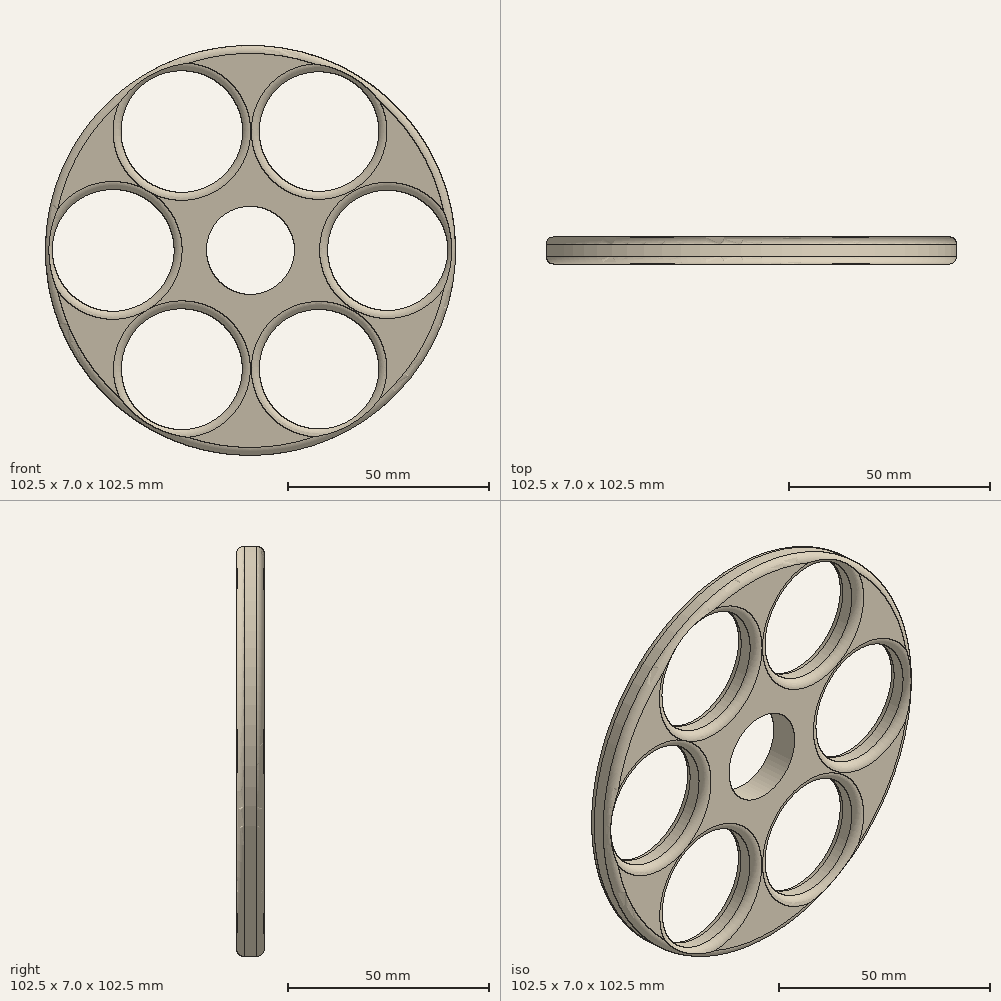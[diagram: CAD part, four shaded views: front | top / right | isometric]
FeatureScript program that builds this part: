
annotation { "Feature Type Name" : "Feature", "Feature Type Description" : "" }
export const myFeature = defineFeature(function(context is Context, id is Id, definition is map)
    precondition{}
    {
        {
            var Q0;
            Q0=qCreatedBy(makeId("Front.planeOp"),FACE);
            var sketch = newSketch(context, id + "F0", { "sketchPlane" : qUnion([Q0])});
            skCircle(sketch, "E0", {"center": v(0, 0) * mm, "radius": 11 * mm});
            skCircle(sketch, "E1.cCircle", {"center": v(0, 0) * mm, "radius": 56.23 * mm, "construction": true});
            skLineSegment(sketch, "E1.0", {"start": v(23.8, -56.23) * mm, "end": v(-23.8, -56.23) * mm});
            skLineSegment(sketch, "E1.1", {"start": v(-36.8, -48.73) * mm, "end": v(-60.6, -7.5) * mm});
            skLineSegment(sketch, "E1.2", {"start": v(-60.6, 7.5) * mm, "end": v(-36.8, 48.73) * mm});
            skLineSegment(sketch, "E1.3", {"start": v(-23.8, 56.23) * mm, "end": v(23.8, 56.23) * mm});
            skLineSegment(sketch, "E1.4", {"start": v(36.8, 48.73) * mm, "end": v(60.6, 7.5) * mm});
            skLineSegment(sketch, "E1.5", {"start": v(60.6, -7.5) * mm, "end": v(36.8, -48.73) * mm});
            skPoint(sketch, "E1.0.midPoint", {"position": v(0, -56.23) * mm});
            skLineSegment(sketch, "E2", {"start": v(-32.47, 56.23) * mm, "end": v(0, 0) * mm});
            skLineSegment(sketch, "E3", {"start": v(-64.93, 0) * mm, "end": v(0, 0) * mm});
            skLineSegment(sketch, "E4", {"start": v(-32.47, -56.23) * mm, "end": v(0, 0) * mm});
            skLineSegment(sketch, "E5", {"start": v(32.47, -56.23) * mm, "end": v(0, 0) * mm});
            skLineSegment(sketch, "E6", {"start": v(64.93, 0) * mm, "end": v(0, 0) * mm});
            skLineSegment(sketch, "E7", {"start": v(32.47, 56.23) * mm, "end": v(0, 0) * mm});
            skLineSegment(sketch, "E8", {"start": v(0, 56.23) * mm, "end": v(0, 0) * mm});
            skLineSegment(sketch, "E9", {"start": v(-48.7, 28.12) * mm, "end": v(0, 0) * mm});
            skLineSegment(sketch, "E10", {"start": v(-48.7, -28.12) * mm, "end": v(0, 0) * mm});
            skLineSegment(sketch, "E11", {"start": v(0, -56.23) * mm, "end": v(0, 0) * mm});
            skLineSegment(sketch, "E12", {"start": v(48.7, -28.12) * mm, "end": v(0, 0) * mm});
            skLineSegment(sketch, "E13", {"start": v(48.7, 28.12) * mm, "end": v(0, 0) * mm});
            skCircle(sketch, "E14.0", {"center": v(0, 0) * mm, "radius": 49.7 * mm});
            skCircle(sketch, "E15.0", {"center": v(0, 0) * mm, "radius": 34.3 * mm});
            skCircle(sketch, "E16", {"center": v(34.3, 0) * mm, "radius": 15.02 * mm});
            skCircle(sketch, "E17", {"center": v(17.15, 29.7) * mm, "radius": 14.94 * mm});
            skCircle(sketch, "E18", {"center": v(-17.15, 29.7) * mm, "radius": 15.2 * mm});
            skCircle(sketch, "E19", {"center": v(-34.3, 0) * mm, "radius": 15.22 * mm});
            skCircle(sketch, "E20", {"center": v(-17.15, -29.7) * mm, "radius": 15.1 * mm});
            skCircle(sketch, "E21", {"center": v(17.15, -29.7) * mm, "radius": 14.93 * mm});
            skPoint(sketch, "E22.visualSharp", {"position": v(32.47, 56.23) * mm});
            skArc(sketch, "E22.filletArc", {"start": v(36.8, 48.73) * mm, "mid": v(31.3, 54.22) * mm, "end": v(23.8, 56.23) * mm});
            skPoint(sketch, "E23.visualSharp", {"position": v(-32.47, 56.23) * mm});
            skArc(sketch, "E23.filletArc", {"start": v(-23.8, 56.23) * mm, "mid": v(-31.3, 54.22) * mm, "end": v(-36.8, 48.73) * mm});
            skPoint(sketch, "E24.visualSharp", {"position": v(-64.93, 0) * mm});
            skArc(sketch, "E24.filletArc", {"start": v(-60.6, 7.5) * mm, "mid": v(-62.61, 0) * mm, "end": v(-60.6, -7.5) * mm});
            skPoint(sketch, "E25.visualSharp", {"position": v(-32.47, -56.23) * mm});
            skArc(sketch, "E25.filletArc", {"start": v(-36.8, -48.73) * mm, "mid": v(-31.3, -54.22) * mm, "end": v(-23.8, -56.23) * mm});
            skPoint(sketch, "E26.visualSharp", {"position": v(32.47, -56.23) * mm});
            skArc(sketch, "E26.filletArc", {"start": v(23.8, -56.23) * mm, "mid": v(31.3, -54.22) * mm, "end": v(36.8, -48.73) * mm});
            skPoint(sketch, "E27.visualSharp", {"position": v(64.93, 0) * mm});
            skArc(sketch, "E27.filletArc", {"start": v(60.6, -7.5) * mm, "mid": v(62.61, 0) * mm, "end": v(60.6, 7.5) * mm});
            skCircle(sketch, "E28", {"center": v(0, 0) * mm, "radius": 51.25 * mm});
            skSolve(sketch);
        }
        {
            var Q0;
            Q0 = qSketchRegion(id + "F0", true);
            extrude(context, id + "F1", {"entities" : qUnion([Q0]), "depth" : 25 * mm, "offsetDistance" : 25 * mm});
        }
        {
            var Q0;
            {var subQ0=sQuery(id+"F0.wireOp",EDGE,"E14.0");var subQ1=sQuery(id+"F0.wireOp",EDGE,"E2");var subQ2=makeQuery(id+"F0.imprint","INTERSECT",VERTEX,{"derivedFrom":[subQ1,subQ0]});Q0=makeQuery(id+"F0.imprint","IMPRINT",FACE,{"disambiguationData":[TD([[makeQuery(id+"F0.imprint","IMPRINT",EDGE,{"disambiguationData":[TD([[subQ2,-1.0]])],"derivedFrom":subQ1}),-1.0]])]});}
            var Q1;
            {var subQ0=sQuery(id+"F0.wireOp",EDGE,"E14.0");var subQ1=sQuery(id+"F0.wireOp",EDGE,"E3");var subQ2=makeQuery(id+"F0.imprint","INTERSECT",VERTEX,{"derivedFrom":[subQ1,subQ0]});Q1=makeQuery(id+"F0.imprint","IMPRINT",FACE,{"disambiguationData":[TD([[makeQuery(id+"F0.imprint","IMPRINT",EDGE,{"disambiguationData":[TD([[subQ2,-1.0]])],"derivedFrom":subQ1}),1.0]])]});}
            var Q2;
            {var subQ5=sQuery(id+"F0.wireOp",EDGE,"E2");var subQ6=sQuery(id+"F0.wireOp",EDGE,"E0");var subQ7=makeQuery(id+"F0.imprint","INTERSECT",VERTEX,{"derivedFrom":[subQ6,subQ5]});Q2=makeQuery(id+"F0.imprint","IMPRINT",FACE,{"disambiguationData":[TD([[makeQuery(id+"F0.imprint","IMPRINT",EDGE,{"disambiguationData":[TD([[subQ7,-1.0]])],"derivedFrom":subQ6}),-1.0]])]});}
            var Q3;
            {var subQ1=sQuery(id+"F0.wireOp",EDGE,"E9");var subQ5=sQuery(id+"F0.wireOp",EDGE,"E0");var subQ6=makeQuery(id+"F0.imprint","INTERSECT",VERTEX,{"derivedFrom":[subQ5,subQ1]});Q3=makeQuery(id+"F0.imprint","IMPRINT",FACE,{"disambiguationData":[TD([[makeQuery(id+"F0.imprint","IMPRINT",EDGE,{"disambiguationData":[TD([[subQ6,-1.0]])],"derivedFrom":subQ5}),-1.0]])]});}
            var Q4;
            {var subQ1=sQuery(id+"F0.wireOp",EDGE,"E8");var subQ5=sQuery(id+"F0.wireOp",EDGE,"E0");var subQ6=makeQuery(id+"F0.imprint","INTERSECT",VERTEX,{"derivedFrom":[subQ5,subQ1]});Q4=makeQuery(id+"F0.imprint","IMPRINT",FACE,{"disambiguationData":[TD([[makeQuery(id+"F0.imprint","IMPRINT",EDGE,{"disambiguationData":[TD([[subQ6,-1.0]])],"derivedFrom":subQ5}),-1.0]])]});}
            var Q5;
            {var subQ5=sQuery(id+"F0.wireOp",EDGE,"E7");var subQ6=sQuery(id+"F0.wireOp",EDGE,"E0");var subQ7=makeQuery(id+"F0.imprint","INTERSECT",VERTEX,{"derivedFrom":[subQ6,subQ5]});Q5=makeQuery(id+"F0.imprint","IMPRINT",FACE,{"disambiguationData":[TD([[makeQuery(id+"F0.imprint","IMPRINT",EDGE,{"disambiguationData":[TD([[subQ7,-1.0]])],"derivedFrom":subQ6}),-1.0]])]});}
            var Q6;
            {var subQ0=sQuery(id+"F0.wireOp",EDGE,"E13");var subQ1=sQuery(id+"F0.wireOp",EDGE,"E0");var subQ2=makeQuery(id+"F0.imprint","INTERSECT",VERTEX,{"derivedFrom":[subQ1,subQ0]});Q6=makeQuery(id+"F0.imprint","IMPRINT",FACE,{"disambiguationData":[TD([[makeQuery(id+"F0.imprint","IMPRINT",EDGE,{"disambiguationData":[TD([[subQ2,-1.0]])],"derivedFrom":subQ1}),-1.0]])]});}
            var Q7;
            {var subQ1=sQuery(id+"F0.wireOp",EDGE,"E13");var subQ5=sQuery(id+"F0.wireOp",EDGE,"E0");var subQ6=makeQuery(id+"F0.imprint","INTERSECT",VERTEX,{"derivedFrom":[subQ5,subQ1]});Q7=makeQuery(id+"F0.imprint","IMPRINT",FACE,{"disambiguationData":[TD([[makeQuery(id+"F0.imprint","IMPRINT",EDGE,{"disambiguationData":[TD([[subQ6,1.0]])],"derivedFrom":subQ5}),-1.0]])]});}
            var Q8;
            {var subQ5=sQuery(id+"F0.wireOp",EDGE,"E14.0");var subQ7=sQuery(id+"F0.wireOp",EDGE,"E6");var subQ8=makeQuery(id+"F0.imprint","INTERSECT",VERTEX,{"derivedFrom":[subQ7,subQ5]});Q8=makeQuery(id+"F0.imprint","IMPRINT",FACE,{"disambiguationData":[TD([[makeQuery(id+"F0.imprint","IMPRINT",EDGE,{"disambiguationData":[TD([[subQ8,-1.0]])],"derivedFrom":subQ7}),-1.0]])]});}
            var Q9;
            {var subQ5=sQuery(id+"F0.wireOp",EDGE,"E14.0");var subQ7=sQuery(id+"F0.wireOp",EDGE,"E7");var subQ8=makeQuery(id+"F0.imprint","INTERSECT",VERTEX,{"derivedFrom":[subQ7,subQ5]});Q9=makeQuery(id+"F0.imprint","IMPRINT",FACE,{"disambiguationData":[TD([[makeQuery(id+"F0.imprint","IMPRINT",EDGE,{"disambiguationData":[TD([[subQ8,-1.0]])],"derivedFrom":subQ7}),1.0]])]});}
            var Q10;
            {var subQ5=sQuery(id+"F0.wireOp",EDGE,"E14.0");var subQ6=sQuery(id+"F0.wireOp",EDGE,"E7");var subQ7=makeQuery(id+"F0.imprint","INTERSECT",VERTEX,{"derivedFrom":[subQ6,subQ5]});Q10=makeQuery(id+"F0.imprint","IMPRINT",FACE,{"disambiguationData":[TD([[makeQuery(id+"F0.imprint","IMPRINT",EDGE,{"disambiguationData":[TD([[subQ7,-1.0]])],"derivedFrom":subQ6}),-1.0]])]});}
            var Q11;
            {var subQ5=sQuery(id+"F0.wireOp",EDGE,"E14.0");var subQ6=sQuery(id+"F0.wireOp",EDGE,"E2");var subQ7=makeQuery(id+"F0.imprint","INTERSECT",VERTEX,{"derivedFrom":[subQ6,subQ5]});Q11=makeQuery(id+"F0.imprint","IMPRINT",FACE,{"disambiguationData":[TD([[makeQuery(id+"F0.imprint","IMPRINT",EDGE,{"disambiguationData":[TD([[subQ7,-1.0]])],"derivedFrom":subQ6}),1.0]])]});}
            var Q12;
            {var subQ0=sQuery(id+"F0.wireOp",EDGE,"E14.0");var subQ1=sQuery(id+"F0.wireOp",EDGE,"E3");var subQ2=makeQuery(id+"F0.imprint","INTERSECT",VERTEX,{"derivedFrom":[subQ1,subQ0]});Q12=makeQuery(id+"F0.imprint","IMPRINT",FACE,{"disambiguationData":[TD([[makeQuery(id+"F0.imprint","IMPRINT",EDGE,{"disambiguationData":[TD([[subQ2,-1.0]])],"derivedFrom":subQ1}),-1.0]])]});}
            var Q13;
            {var subQ1=sQuery(id+"F0.wireOp",EDGE,"E0");var subQ7=sQuery(id+"F0.wireOp",EDGE,"E3");var subQ8=makeQuery(id+"F0.imprint","INTERSECT",VERTEX,{"derivedFrom":[subQ1,subQ7]});Q13=makeQuery(id+"F0.imprint","IMPRINT",FACE,{"disambiguationData":[TD([[makeQuery(id+"F0.imprint","IMPRINT",EDGE,{"disambiguationData":[TD([[subQ8,-1.0]])],"derivedFrom":subQ1}),-1.0]])]});}
            var Q14;
            {var subQ1=sQuery(id+"F0.wireOp",EDGE,"E10");var subQ5=sQuery(id+"F0.wireOp",EDGE,"E0");var subQ6=makeQuery(id+"F0.imprint","INTERSECT",VERTEX,{"derivedFrom":[subQ5,subQ1]});Q14=makeQuery(id+"F0.imprint","IMPRINT",FACE,{"disambiguationData":[TD([[makeQuery(id+"F0.imprint","IMPRINT",EDGE,{"disambiguationData":[TD([[subQ6,-1.0]])],"derivedFrom":subQ5}),-1.0]])]});}
            var Q15;
            {var subQ5=sQuery(id+"F0.wireOp",EDGE,"E14.0");var subQ6=sQuery(id+"F0.wireOp",EDGE,"E4");var subQ7=makeQuery(id+"F0.imprint","INTERSECT",VERTEX,{"derivedFrom":[subQ6,subQ5]});Q15=makeQuery(id+"F0.imprint","IMPRINT",FACE,{"disambiguationData":[TD([[makeQuery(id+"F0.imprint","IMPRINT",EDGE,{"disambiguationData":[TD([[subQ7,-1.0]])],"derivedFrom":subQ6}),1.0]])]});}
            var Q16;
            {var subQ5=sQuery(id+"F0.wireOp",EDGE,"E14.0");var subQ7=sQuery(id+"F0.wireOp",EDGE,"E4");var subQ8=makeQuery(id+"F0.imprint","INTERSECT",VERTEX,{"derivedFrom":[subQ7,subQ5]});Q16=makeQuery(id+"F0.imprint","IMPRINT",FACE,{"disambiguationData":[TD([[makeQuery(id+"F0.imprint","IMPRINT",EDGE,{"disambiguationData":[TD([[subQ8,-1.0]])],"derivedFrom":subQ7}),-1.0]])]});}
            var Q17;
            {var subQ5=sQuery(id+"F0.wireOp",EDGE,"E14.0");var subQ6=sQuery(id+"F0.wireOp",EDGE,"E5");var subQ7=makeQuery(id+"F0.imprint","INTERSECT",VERTEX,{"derivedFrom":[subQ6,subQ5]});Q17=makeQuery(id+"F0.imprint","IMPRINT",FACE,{"disambiguationData":[TD([[makeQuery(id+"F0.imprint","IMPRINT",EDGE,{"disambiguationData":[TD([[subQ7,-1.0]])],"derivedFrom":subQ6}),1.0]])]});}
            var Q18;
            {var subQ1=sQuery(id+"F0.wireOp",EDGE,"E0");var subQ6=sQuery(id+"F0.wireOp",EDGE,"E11");var subQ9=makeQuery(id+"F0.imprint","INTERSECT",VERTEX,{"derivedFrom":[subQ1,subQ6]});Q18=makeQuery(id+"F0.imprint","IMPRINT",FACE,{"disambiguationData":[TD([[makeQuery(id+"F0.imprint","IMPRINT",EDGE,{"disambiguationData":[TD([[subQ9,-1.0]])],"derivedFrom":subQ1}),-1.0]])]});}
            var Q19;
            {var subQ1=sQuery(id+"F0.wireOp",EDGE,"E0");var subQ5=sQuery(id+"F0.wireOp",EDGE,"E4");var subQ6=makeQuery(id+"F0.imprint","INTERSECT",VERTEX,{"derivedFrom":[subQ1,subQ5]});Q19=makeQuery(id+"F0.imprint","IMPRINT",FACE,{"disambiguationData":[TD([[makeQuery(id+"F0.imprint","IMPRINT",EDGE,{"disambiguationData":[TD([[subQ6,-1.0]])],"derivedFrom":subQ1}),-1.0]])]});}
            var Q20;
            {var subQ5=sQuery(id+"F0.wireOp",EDGE,"E0");var subQ7=sQuery(id+"F0.wireOp",EDGE,"E5");var subQ8=makeQuery(id+"F0.imprint","INTERSECT",VERTEX,{"derivedFrom":[subQ5,subQ7]});Q20=makeQuery(id+"F0.imprint","IMPRINT",FACE,{"disambiguationData":[TD([[makeQuery(id+"F0.imprint","IMPRINT",EDGE,{"disambiguationData":[TD([[subQ8,-1.0]])],"derivedFrom":subQ5}),-1.0]])]});}
            var Q21;
            {var subQ5=sQuery(id+"F0.wireOp",EDGE,"E6");var subQ6=sQuery(id+"F0.wireOp",EDGE,"E0");var subQ7=makeQuery(id+"F0.imprint","INTERSECT",VERTEX,{"derivedFrom":[subQ6,subQ5]});Q21=makeQuery(id+"F0.imprint","IMPRINT",FACE,{"disambiguationData":[TD([[makeQuery(id+"F0.imprint","IMPRINT",EDGE,{"disambiguationData":[TD([[subQ7,1.0]])],"derivedFrom":subQ6}),-1.0]])]});}
            var Q22;
            {var subQ5=sQuery(id+"F0.wireOp",EDGE,"E14.0");var subQ6=sQuery(id+"F0.wireOp",EDGE,"E6");var subQ7=makeQuery(id+"F0.imprint","INTERSECT",VERTEX,{"derivedFrom":[subQ6,subQ5]});Q22=makeQuery(id+"F0.imprint","IMPRINT",FACE,{"disambiguationData":[TD([[makeQuery(id+"F0.imprint","IMPRINT",EDGE,{"disambiguationData":[TD([[subQ7,-1.0]])],"derivedFrom":subQ6}),1.0]])]});}
            var Q23;
            {var subQ0=sQuery(id+"F0.wireOp",EDGE,"E14.0");var subQ1=sQuery(id+"F0.wireOp",EDGE,"E5");var subQ2=makeQuery(id+"F0.imprint","INTERSECT",VERTEX,{"derivedFrom":[subQ1,subQ0]});Q23=makeQuery(id+"F0.imprint","IMPRINT",FACE,{"disambiguationData":[TD([[makeQuery(id+"F0.imprint","IMPRINT",EDGE,{"disambiguationData":[TD([[subQ2,-1.0]])],"derivedFrom":subQ1}),-1.0]])]});}
            extrude(context, id + "F2", {"entities" : qUnion([Q0, Q1, Q2, Q3, Q4, Q5, Q6, Q7, Q8, Q9, Q10, Q11, Q12, Q13, Q14, Q15, Q16, Q17, Q18, Q19, Q20, Q21, Q22, Q23]), "operationType" : NewBodyOperationType.ADD, "depth" : 7 * mm, "offsetDistance" : 25 * mm});
        }
        {
            var Q0;
            Q0=makeQuery(id+"F1.opExtrude","CAP_FACE",FACE,{"disambiguationData":[OSD([sQuery(id+"F0.wireOp",EDGE,"E1.0"),sQuery(id+"F0.wireOp",EDGE,"E1.1"),sQuery(id+"F0.wireOp",EDGE,"E1.2"),sQuery(id+"F0.wireOp",EDGE,"E1.3"),sQuery(id+"F0.wireOp",EDGE,"E1.4"),sQuery(id+"F0.wireOp",EDGE,"E1.5"),sQuery(id+"F0.wireOp",EDGE,"E14.0"),sQuery(id+"F0.wireOp",EDGE,"E22.filletArc"),sQuery(id+"F0.wireOp",EDGE,"E23.filletArc"),sQuery(id+"F0.wireOp",EDGE,"E24.filletArc"),sQuery(id+"F0.wireOp",EDGE,"E25.filletArc"),sQuery(id+"F0.wireOp",EDGE,"E26.filletArc"),sQuery(id+"F0.wireOp",EDGE,"E27.filletArc")])],"isStart":false});
            extrude(context, id + "F3", {"entities" : qUnion([Q0]), "operationType" : NewBodyOperationType.REMOVE, "oppositeDirection" : true, "depth" : 25 * mm, "offsetDistance" : 25 * mm});
        }
        {
            var Q0;
            Q0 = qSketchRegion(id + "F0", true);
            var Q1;
            {var subQ0=sQuery(id+"F0.wireOp",EDGE,"E28");var subQ1=sQuery(id+"F0.wireOp",EDGE,"E2");var subQ2=makeQuery(id+"F0.imprint","INTERSECT",VERTEX,{"derivedFrom":[subQ1,subQ0]});Q1=makeQuery(id+"F0.imprint","IMPRINT",FACE,{"disambiguationData":[TD([[makeQuery(id+"F0.imprint","IMPRINT",EDGE,{"disambiguationData":[TD([[subQ2,-1.0]])],"derivedFrom":subQ1}),1.0]])]});}
            var Q2;
            {var subQ0=sQuery(id+"F0.wireOp",EDGE,"E28");var subQ1=sQuery(id+"F0.wireOp",EDGE,"E2");var subQ2=makeQuery(id+"F0.imprint","INTERSECT",VERTEX,{"derivedFrom":[subQ1,subQ0]});Q2=makeQuery(id+"F0.imprint","IMPRINT",FACE,{"disambiguationData":[TD([[makeQuery(id+"F0.imprint","IMPRINT",EDGE,{"disambiguationData":[TD([[subQ2,-1.0]])],"derivedFrom":subQ1}),-1.0]])]});}
            var Q3;
            {var subQ0=sQuery(id+"F0.wireOp",EDGE,"E28");var subQ1=sQuery(id+"F0.wireOp",EDGE,"E3");var subQ2=makeQuery(id+"F0.imprint","INTERSECT",VERTEX,{"derivedFrom":[subQ1,subQ0]});Q3=makeQuery(id+"F0.imprint","IMPRINT",FACE,{"disambiguationData":[TD([[makeQuery(id+"F0.imprint","IMPRINT",EDGE,{"disambiguationData":[TD([[subQ2,-1.0]])],"derivedFrom":subQ1}),1.0]])]});}
            var Q4;
            {var subQ0=sQuery(id+"F0.wireOp",EDGE,"E28");var subQ1=sQuery(id+"F0.wireOp",EDGE,"E3");var subQ2=makeQuery(id+"F0.imprint","INTERSECT",VERTEX,{"derivedFrom":[subQ1,subQ0]});Q4=makeQuery(id+"F0.imprint","IMPRINT",FACE,{"disambiguationData":[TD([[makeQuery(id+"F0.imprint","IMPRINT",EDGE,{"disambiguationData":[TD([[subQ2,-1.0]])],"derivedFrom":subQ1}),-1.0]])]});}
            var Q5;
            {var subQ0=sQuery(id+"F0.wireOp",EDGE,"E28");var subQ1=sQuery(id+"F0.wireOp",EDGE,"E7");var subQ2=makeQuery(id+"F0.imprint","INTERSECT",VERTEX,{"derivedFrom":[subQ1,subQ0]});Q5=makeQuery(id+"F0.imprint","IMPRINT",FACE,{"disambiguationData":[TD([[makeQuery(id+"F0.imprint","IMPRINT",EDGE,{"disambiguationData":[TD([[subQ2,-1.0]])],"derivedFrom":subQ1}),-1.0]])]});}
            var Q6;
            {var subQ0=sQuery(id+"F0.wireOp",EDGE,"E28");var subQ1=sQuery(id+"F0.wireOp",EDGE,"E7");var subQ2=makeQuery(id+"F0.imprint","INTERSECT",VERTEX,{"derivedFrom":[subQ1,subQ0]});Q6=makeQuery(id+"F0.imprint","IMPRINT",FACE,{"disambiguationData":[TD([[makeQuery(id+"F0.imprint","IMPRINT",EDGE,{"disambiguationData":[TD([[subQ2,-1.0]])],"derivedFrom":subQ1}),1.0]])]});}
            var Q7;
            {var subQ0=sQuery(id+"F0.wireOp",EDGE,"E28");var subQ1=sQuery(id+"F0.wireOp",EDGE,"E6");var subQ2=makeQuery(id+"F0.imprint","INTERSECT",VERTEX,{"derivedFrom":[subQ1,subQ0]});Q7=makeQuery(id+"F0.imprint","IMPRINT",FACE,{"disambiguationData":[TD([[makeQuery(id+"F0.imprint","IMPRINT",EDGE,{"disambiguationData":[TD([[subQ2,-1.0]])],"derivedFrom":subQ1}),-1.0]])]});}
            var Q8;
            {var subQ0=sQuery(id+"F0.wireOp",EDGE,"E28");var subQ1=sQuery(id+"F0.wireOp",EDGE,"E6");var subQ2=makeQuery(id+"F0.imprint","INTERSECT",VERTEX,{"derivedFrom":[subQ1,subQ0]});Q8=makeQuery(id+"F0.imprint","IMPRINT",FACE,{"disambiguationData":[TD([[makeQuery(id+"F0.imprint","IMPRINT",EDGE,{"disambiguationData":[TD([[subQ2,-1.0]])],"derivedFrom":subQ1}),1.0]])]});}
            var Q9;
            {var subQ0=sQuery(id+"F0.wireOp",EDGE,"E28");var subQ1=sQuery(id+"F0.wireOp",EDGE,"E5");var subQ2=makeQuery(id+"F0.imprint","INTERSECT",VERTEX,{"derivedFrom":[subQ1,subQ0]});Q9=makeQuery(id+"F0.imprint","IMPRINT",FACE,{"disambiguationData":[TD([[makeQuery(id+"F0.imprint","IMPRINT",EDGE,{"disambiguationData":[TD([[subQ2,-1.0]])],"derivedFrom":subQ1}),-1.0]])]});}
            var Q10;
            {var subQ0=sQuery(id+"F0.wireOp",EDGE,"E28");var subQ1=sQuery(id+"F0.wireOp",EDGE,"E5");var subQ2=makeQuery(id+"F0.imprint","INTERSECT",VERTEX,{"derivedFrom":[subQ1,subQ0]});Q10=makeQuery(id+"F0.imprint","IMPRINT",FACE,{"disambiguationData":[TD([[makeQuery(id+"F0.imprint","IMPRINT",EDGE,{"disambiguationData":[TD([[subQ2,-1.0]])],"derivedFrom":subQ1}),1.0]])]});}
            var Q11;
            {var subQ0=sQuery(id+"F0.wireOp",EDGE,"E28");var subQ1=sQuery(id+"F0.wireOp",EDGE,"E4");var subQ2=makeQuery(id+"F0.imprint","INTERSECT",VERTEX,{"derivedFrom":[subQ1,subQ0]});Q11=makeQuery(id+"F0.imprint","IMPRINT",FACE,{"disambiguationData":[TD([[makeQuery(id+"F0.imprint","IMPRINT",EDGE,{"disambiguationData":[TD([[subQ2,-1.0]])],"derivedFrom":subQ1}),-1.0]])]});}
            var Q12;
            {var subQ0=sQuery(id+"F0.wireOp",EDGE,"E28");var subQ1=sQuery(id+"F0.wireOp",EDGE,"E4");var subQ2=makeQuery(id+"F0.imprint","INTERSECT",VERTEX,{"derivedFrom":[subQ1,subQ0]});Q12=makeQuery(id+"F0.imprint","IMPRINT",FACE,{"disambiguationData":[TD([[makeQuery(id+"F0.imprint","IMPRINT",EDGE,{"disambiguationData":[TD([[subQ2,-1.0]])],"derivedFrom":subQ1}),1.0]])]});}
            extrude(context, id + "F4", {"entities" : qUnion([Q0, Q1, Q2, Q3, Q4, Q5, Q6, Q7, Q8, Q9, Q10, Q11, Q12]), "operationType" : NewBodyOperationType.REMOVE, "endBound" : BoundingType.THROUGH_ALL, "depth" : 25 * mm, "offsetDistance" : 25 * mm});
        }
        {
            var Q0;
            {var subQ0=sQuery(id+"F0.wireOp",EDGE,"E28");var subQ1=sQuery(id+"F0.wireOp",EDGE,"E2");var subQ2=makeQuery(id+"F0.imprint","INTERSECT",VERTEX,{"derivedFrom":[subQ1,subQ0]});Q0=makeQuery(id+"F0.imprint","IMPRINT",FACE,{"disambiguationData":[TD([[makeQuery(id+"F0.imprint","IMPRINT",EDGE,{"disambiguationData":[TD([[subQ2,-1.0]])],"derivedFrom":subQ1}),-1.0]])]});}
            var Q1;
            {var subQ0=sQuery(id+"F0.wireOp",EDGE,"E28");var subQ1=sQuery(id+"F0.wireOp",EDGE,"E2");var subQ2=makeQuery(id+"F0.imprint","INTERSECT",VERTEX,{"derivedFrom":[subQ1,subQ0]});Q1=makeQuery(id+"F0.imprint","IMPRINT",FACE,{"disambiguationData":[TD([[makeQuery(id+"F0.imprint","IMPRINT",EDGE,{"disambiguationData":[TD([[subQ2,-1.0]])],"derivedFrom":subQ1}),1.0]])]});}
            var Q2;
            {var subQ0=sQuery(id+"F0.wireOp",EDGE,"E28");var subQ1=sQuery(id+"F0.wireOp",EDGE,"E3");var subQ2=makeQuery(id+"F0.imprint","INTERSECT",VERTEX,{"derivedFrom":[subQ1,subQ0]});Q2=makeQuery(id+"F0.imprint","IMPRINT",FACE,{"disambiguationData":[TD([[makeQuery(id+"F0.imprint","IMPRINT",EDGE,{"disambiguationData":[TD([[subQ2,-1.0]])],"derivedFrom":subQ1}),1.0]])]});}
            var Q3;
            {var subQ0=sQuery(id+"F0.wireOp",EDGE,"E28");var subQ1=sQuery(id+"F0.wireOp",EDGE,"E3");var subQ2=makeQuery(id+"F0.imprint","INTERSECT",VERTEX,{"derivedFrom":[subQ1,subQ0]});Q3=makeQuery(id+"F0.imprint","IMPRINT",FACE,{"disambiguationData":[TD([[makeQuery(id+"F0.imprint","IMPRINT",EDGE,{"disambiguationData":[TD([[subQ2,-1.0]])],"derivedFrom":subQ1}),-1.0]])]});}
            var Q4;
            {var subQ0=sQuery(id+"F0.wireOp",EDGE,"E28");var subQ1=sQuery(id+"F0.wireOp",EDGE,"E4");var subQ2=makeQuery(id+"F0.imprint","INTERSECT",VERTEX,{"derivedFrom":[subQ1,subQ0]});Q4=makeQuery(id+"F0.imprint","IMPRINT",FACE,{"disambiguationData":[TD([[makeQuery(id+"F0.imprint","IMPRINT",EDGE,{"disambiguationData":[TD([[subQ2,-1.0]])],"derivedFrom":subQ1}),1.0]])]});}
            var Q5;
            {var subQ0=sQuery(id+"F0.wireOp",EDGE,"E28");var subQ1=sQuery(id+"F0.wireOp",EDGE,"E4");var subQ2=makeQuery(id+"F0.imprint","INTERSECT",VERTEX,{"derivedFrom":[subQ1,subQ0]});Q5=makeQuery(id+"F0.imprint","IMPRINT",FACE,{"disambiguationData":[TD([[makeQuery(id+"F0.imprint","IMPRINT",EDGE,{"disambiguationData":[TD([[subQ2,-1.0]])],"derivedFrom":subQ1}),-1.0]])]});}
            var Q6;
            {var subQ0=sQuery(id+"F0.wireOp",EDGE,"E28");var subQ1=sQuery(id+"F0.wireOp",EDGE,"E5");var subQ2=makeQuery(id+"F0.imprint","INTERSECT",VERTEX,{"derivedFrom":[subQ1,subQ0]});Q6=makeQuery(id+"F0.imprint","IMPRINT",FACE,{"disambiguationData":[TD([[makeQuery(id+"F0.imprint","IMPRINT",EDGE,{"disambiguationData":[TD([[subQ2,-1.0]])],"derivedFrom":subQ1}),1.0]])]});}
            var Q7;
            {var subQ0=sQuery(id+"F0.wireOp",EDGE,"E28");var subQ1=sQuery(id+"F0.wireOp",EDGE,"E5");var subQ2=makeQuery(id+"F0.imprint","INTERSECT",VERTEX,{"derivedFrom":[subQ1,subQ0]});Q7=makeQuery(id+"F0.imprint","IMPRINT",FACE,{"disambiguationData":[TD([[makeQuery(id+"F0.imprint","IMPRINT",EDGE,{"disambiguationData":[TD([[subQ2,-1.0]])],"derivedFrom":subQ1}),-1.0]])]});}
            var Q8;
            {var subQ0=sQuery(id+"F0.wireOp",EDGE,"E28");var subQ1=sQuery(id+"F0.wireOp",EDGE,"E6");var subQ2=makeQuery(id+"F0.imprint","INTERSECT",VERTEX,{"derivedFrom":[subQ1,subQ0]});Q8=makeQuery(id+"F0.imprint","IMPRINT",FACE,{"disambiguationData":[TD([[makeQuery(id+"F0.imprint","IMPRINT",EDGE,{"disambiguationData":[TD([[subQ2,-1.0]])],"derivedFrom":subQ1}),1.0]])]});}
            var Q9;
            {var subQ0=sQuery(id+"F0.wireOp",EDGE,"E28");var subQ1=sQuery(id+"F0.wireOp",EDGE,"E6");var subQ2=makeQuery(id+"F0.imprint","INTERSECT",VERTEX,{"derivedFrom":[subQ1,subQ0]});Q9=makeQuery(id+"F0.imprint","IMPRINT",FACE,{"disambiguationData":[TD([[makeQuery(id+"F0.imprint","IMPRINT",EDGE,{"disambiguationData":[TD([[subQ2,-1.0]])],"derivedFrom":subQ1}),-1.0]])]});}
            var Q10;
            {var subQ0=sQuery(id+"F0.wireOp",EDGE,"E28");var subQ1=sQuery(id+"F0.wireOp",EDGE,"E7");var subQ2=makeQuery(id+"F0.imprint","INTERSECT",VERTEX,{"derivedFrom":[subQ1,subQ0]});Q10=makeQuery(id+"F0.imprint","IMPRINT",FACE,{"disambiguationData":[TD([[makeQuery(id+"F0.imprint","IMPRINT",EDGE,{"disambiguationData":[TD([[subQ2,-1.0]])],"derivedFrom":subQ1}),1.0]])]});}
            var Q11;
            {var subQ0=sQuery(id+"F0.wireOp",EDGE,"E28");var subQ1=sQuery(id+"F0.wireOp",EDGE,"E7");var subQ2=makeQuery(id+"F0.imprint","INTERSECT",VERTEX,{"derivedFrom":[subQ1,subQ0]});Q11=makeQuery(id+"F0.imprint","IMPRINT",FACE,{"disambiguationData":[TD([[makeQuery(id+"F0.imprint","IMPRINT",EDGE,{"disambiguationData":[TD([[subQ2,-1.0]])],"derivedFrom":subQ1}),-1.0]])]});}
            extrude(context, id + "F5", {"entities" : qUnion([Q0, Q1, Q2, Q3, Q4, Q5, Q6, Q7, Q8, Q9, Q10, Q11]), "operationType" : NewBodyOperationType.ADD, "depth" : 7 * mm, "offsetDistance" : 25 * mm});
        }
        {
            var Q0;
            Q0=makeQuery(id+"F5.opExtrude","CAP_EDGE",EDGE,{"disambiguationData":[OSD([sQuery(id+"F0.wireOp",EDGE,"E28")])],"isStart":false});
            var Q1;
            Q1=makeQuery(id+"F2.opExtrude","CAP_EDGE",EDGE,{"disambiguationData":[OSD([sQuery(id+"F0.wireOp",EDGE,"E18")])],"isStart":false});
            var Q2;
            Q2=makeQuery(id+"F2.opExtrude","CAP_EDGE",EDGE,{"disambiguationData":[OSD([sQuery(id+"F0.wireOp",EDGE,"E19")])],"isStart":false});
            var Q3;
            Q3=makeQuery(id+"F2.opExtrude","CAP_EDGE",EDGE,{"disambiguationData":[OSD([sQuery(id+"F0.wireOp",EDGE,"E20")])],"isStart":false});
            var Q4;
            Q4=makeQuery(id+"F2.opExtrude","CAP_EDGE",EDGE,{"disambiguationData":[OSD([sQuery(id+"F0.wireOp",EDGE,"E21")])],"isStart":false});
            var Q5;
            Q5=makeQuery(id+"F2.opExtrude","CAP_EDGE",EDGE,{"disambiguationData":[OSD([sQuery(id+"F0.wireOp",EDGE,"E16")])],"isStart":false});
            var Q6;
            Q6=makeQuery(id+"F2.opExtrude","CAP_EDGE",EDGE,{"disambiguationData":[OSD([sQuery(id+"F0.wireOp",EDGE,"E17")])],"isStart":false});
            fillet(context, id + "F6", {"entities" : qUnion([Q0, Q1, Q2, Q3, Q4, Q5, Q6]), "radius" : 2 * mm, "tangentPropagation" : true, "allowEdgeOverflow" : false});
        }
        {
            var Q0;
            Q0=makeQuery(id+"F5.opExtrude","CAP_EDGE",EDGE,{"disambiguationData":[OSD([sQuery(id+"F0.wireOp",EDGE,"E28")])],"isStart":true});
            var Q1;
            Q1=makeQuery(id+"F2.opExtrude","CAP_EDGE",EDGE,{"disambiguationData":[OSD([sQuery(id+"F0.wireOp",EDGE,"E17")])],"isStart":true});
            var Q2;
            Q2=makeQuery(id+"F2.opExtrude","CAP_EDGE",EDGE,{"disambiguationData":[OSD([sQuery(id+"F0.wireOp",EDGE,"E16")])],"isStart":true});
            var Q3;
            Q3=makeQuery(id+"F2.opExtrude","CAP_EDGE",EDGE,{"disambiguationData":[OSD([sQuery(id+"F0.wireOp",EDGE,"E21")])],"isStart":true});
            var Q4;
            Q4=makeQuery(id+"F2.opExtrude","CAP_EDGE",EDGE,{"disambiguationData":[OSD([sQuery(id+"F0.wireOp",EDGE,"E20")])],"isStart":true});
            var Q5;
            Q5=makeQuery(id+"F2.opExtrude","CAP_EDGE",EDGE,{"disambiguationData":[OSD([sQuery(id+"F0.wireOp",EDGE,"E19")])],"isStart":true});
            var Q6;
            Q6=makeQuery(id+"F2.opExtrude","CAP_EDGE",EDGE,{"disambiguationData":[OSD([sQuery(id+"F0.wireOp",EDGE,"E18")])],"isStart":true});
            fillet(context, id + "F7", {"entities" : qUnion([Q0, Q1, Q2, Q3, Q4, Q5, Q6]), "radius" : 2 * mm, "tangentPropagation" : true, "allowEdgeOverflow" : false});
        }
    });
